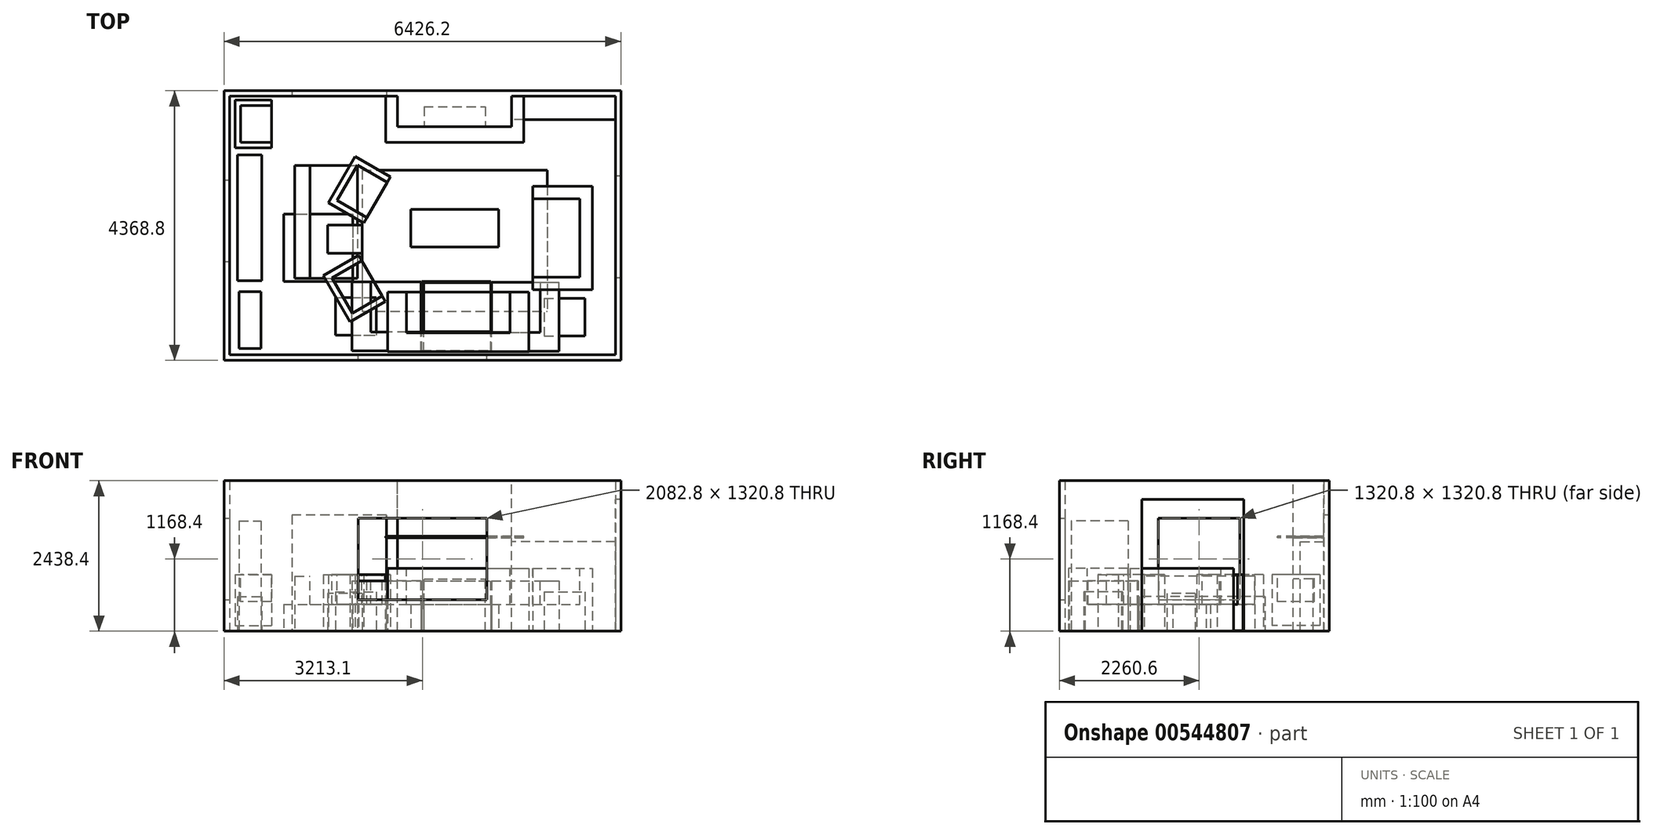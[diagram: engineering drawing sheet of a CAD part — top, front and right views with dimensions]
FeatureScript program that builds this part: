
annotation { "Feature Type Name" : "Feature", "Feature Type Description" : "" }
export const myFeature = defineFeature(function(context is Context, id is Id, definition is map)
    precondition{}
    {
        {
            var Q0;
            Q0=qCreatedBy(makeId("Top.planeOp"),FACE);
            var sketch = newSketch(context, id + "F0", { "sketchPlane" : qUnion([Q0])});
            skLineSegment(sketch, "E0.bottom", {"start": v(0, 0) * mm, "end": v(6248.4, 0) * mm});
            skLineSegment(sketch, "E0.top", {"start": v(0, -4191) * mm, "end": v(6248.4, -4191) * mm});
            skLineSegment(sketch, "E0.left", {"start": v(0, 0) * mm, "end": v(0, -4191) * mm});
            skLineSegment(sketch, "E0.right", {"start": v(6248.4, 0) * mm, "end": v(6248.4, -4191) * mm});
            skLineSegment(sketch, "E1.0", {"start": v(-88.9, 88.9) * mm, "end": v(6337.3, 88.9) * mm});
            skLineSegment(sketch, "E1.1", {"start": v(-88.9, 88.9) * mm, "end": v(-88.9, -4279.9) * mm});
            skLineSegment(sketch, "E1.2", {"start": v(-88.9, -4279.9) * mm, "end": v(6337.3, -4279.9) * mm});
            skLineSegment(sketch, "E1.3", {"start": v(6337.3, 88.9) * mm, "end": v(6337.3, -4279.9) * mm});
            skSolve(sketch);
        }
        {
            var Q0;
            Q0 = qSketchRegion(id + "F0", true);
            extrude(context, id + "F1", {"entities" : qUnion([Q0]), "depth" : 2438.4 * mm, "offsetDistance" : 25.4 * mm});
        }
        {
            var Q0;
            Q0=makeQuery(id+"F1.opExtrude","SWEPT_FACE",FACE,{"disambiguationData":[OSD([sQuery(id+"F0.wireOp",EDGE,"E0.bottom")])]});
            var sketch = newSketch(context, id + "F2", { "sketchPlane" : qUnion([Q0])});
            skLineSegment(sketch, "E2.bottom", {"start": v(1016, 0) * mm, "end": v(2540, 0) * mm});
            skLineSegment(sketch, "E2.top", {"start": v(1016, 1879.6) * mm, "end": v(2540, 1879.6) * mm});
            skLineSegment(sketch, "E2.left", {"start": v(1016, 0) * mm, "end": v(1016, 1879.6) * mm});
            skLineSegment(sketch, "E2.right", {"start": v(2540, 0) * mm, "end": v(2540, 1879.6) * mm});
            skSolve(sketch);
        }
        {
            var Q0;
            Q0 = qSketchRegion(id + "F2", true);
            extrude(context, id + "F3", {"entities" : qUnion([Q0]), "operationType" : NewBodyOperationType.REMOVE, "oppositeDirection" : true, "depth" : 101.6 * mm, "offsetDistance" : 25.4 * mm});
        }
        {
            var Q0;
            Q0=makeQuery(id+"F1.opExtrude","SWEPT_FACE",FACE,{"disambiguationData":[OSD([sQuery(id+"F0.wireOp",EDGE,"E0.bottom")])]});
            var sketch = newSketch(context, id + "F4", { "sketchPlane" : qUnion([Q0])});
            skLineSegment(sketch, "E3.bottom", {"start": v(2717.8, 0) * mm, "end": v(4572, 0) * mm});
            skLineSegment(sketch, "E3.top", {"start": v(2717.8, 2438.4) * mm, "end": v(4572, 2438.4) * mm});
            skLineSegment(sketch, "E3.left", {"start": v(2717.8, 0) * mm, "end": v(2717.8, 2438.4) * mm});
            skLineSegment(sketch, "E3.right", {"start": v(4572, 0) * mm, "end": v(4572, 2438.4) * mm});
            skSolve(sketch);
        }
        {
            var Q0;
            Q0 = qSketchRegion(id + "F4", true);
            extrude(context, id + "F5", {"entities" : qUnion([Q0]), "operationType" : NewBodyOperationType.ADD, "depth" : 495.3 * mm, "offsetDistance" : 25.4 * mm});
        }
        {
            var Q0;
            {var subQ0=sQuery(id+"F0.wireOp",EDGE,"E0.right");var subQ7=sQuery(id+"F0.wireOp",EDGE,"E0.bottom");Q0=makeQuery(id+"F5.boolean.opBoolean","SPLIT",FACE,{"disambiguationData":[TD([makeQuery(id+"F1.opExtrude","SWEPT_FACE",FACE,{"disambiguationData":[OSD([subQ0])]})])],"derivedFrom":makeQuery(id+"F1.opExtrude","SWEPT_FACE",FACE,{"disambiguationData":[OSD([subQ7])]})});}
            var sketch = newSketch(context, id + "F6", { "sketchPlane" : qUnion([Q0])});
            skLineSegment(sketch, "E4.bottom", {"start": v(6248.4, 0) * mm, "end": v(4572, 0) * mm});
            skLineSegment(sketch, "E4.top", {"start": v(6248.4, 1447.8) * mm, "end": v(4572, 1447.8) * mm});
            skLineSegment(sketch, "E4.left", {"start": v(6248.4, 0) * mm, "end": v(6248.4, 1447.8) * mm});
            skLineSegment(sketch, "E4.right", {"start": v(4572, 0) * mm, "end": v(4572, 1447.8) * mm});
            skSolve(sketch);
        }
        {
            var Q0;
            Q0=makeQuery(id+"F6.imprint","IMPRINT",FACE,{"disambiguationData":[TD([[makeQuery(id+"F6.imprint","IMPRINT",EDGE,{"derivedFrom":sQuery(id+"F6.wireOp",EDGE,"E4.bottom")}),1.0]])]});
            extrude(context, id + "F7", {"entities" : qUnion([Q0]), "operationType" : NewBodyOperationType.ADD, "depth" : 381 * mm, "offsetDistance" : 25.4 * mm});
        }
        {
            var Q0;
            Q0=makeQuery(id+"F1.opExtrude","SWEPT_FACE",FACE,{"disambiguationData":[OSD([sQuery(id+"F0.wireOp",EDGE,"E0.top")])]});
            var sketch = newSketch(context, id + "F8", { "sketchPlane" : qUnion([Q0])});
            skLineSegment(sketch, "E5.bottom", {"start": v(-4165.6, 1828.8) * mm, "end": v(-2082.8, 1828.8) * mm});
            skLineSegment(sketch, "E5.top", {"start": v(-4165.6, 508) * mm, "end": v(-2082.8, 508) * mm});
            skLineSegment(sketch, "E5.left", {"start": v(-4165.6, 1828.8) * mm, "end": v(-4165.6, 508) * mm});
            skLineSegment(sketch, "E5.right", {"start": v(-2082.8, 1828.8) * mm, "end": v(-2082.8, 508) * mm});
            skSolve(sketch);
        }
        {
            var Q0;
            Q0=makeQuery(id+"F8.imprint","IMPRINT",FACE,{"disambiguationData":[TD([[makeQuery(id+"F8.imprint","IMPRINT",EDGE,{"derivedFrom":sQuery(id+"F8.wireOp",EDGE,"E5.bottom")}),-1.0]])]});
            extrude(context, id + "F9", {"entities" : qUnion([Q0]), "operationType" : NewBodyOperationType.REMOVE, "endBound" : BoundingType.THROUGH_ALL, "oppositeDirection" : true, "depth" : 25.4 * mm, "offsetDistance" : 25.4 * mm});
        }
        {
            var Q0;
            Q0=makeQuery(id+"F1.opExtrude","SWEPT_FACE",FACE,{"disambiguationData":[OSD([sQuery(id+"F0.wireOp",EDGE,"E0.right")])]});
            var sketch = newSketch(context, id + "F10", { "sketchPlane" : qUnion([Q0])});
            skLineSegment(sketch, "E6.bottom", {"start": v(1295.4, 0) * mm, "end": v(2946.4, 0) * mm});
            skLineSegment(sketch, "E6.top", {"start": v(1295.4, 2133.6) * mm, "end": v(2946.4, 2133.6) * mm});
            skLineSegment(sketch, "E6.left", {"start": v(1295.4, 0) * mm, "end": v(1295.4, 2133.6) * mm});
            skLineSegment(sketch, "E6.right", {"start": v(2946.4, 0) * mm, "end": v(2946.4, 2133.6) * mm});
            skSolve(sketch);
        }
        {
            var Q0;
            Q0=makeQuery(id+"F10.imprint","IMPRINT",FACE,{"disambiguationData":[TD([[makeQuery(id+"F10.imprint","IMPRINT",EDGE,{"derivedFrom":sQuery(id+"F10.wireOp",EDGE,"E6.bottom")}),1.0]])]});
            extrude(context, id + "F11", {"entities" : qUnion([Q0]), "operationType" : NewBodyOperationType.REMOVE, "endBound" : BoundingType.THROUGH_ALL, "oppositeDirection" : true, "depth" : 25.4 * mm, "offsetDistance" : 25.4 * mm});
        }
        {
            var Q0;
            Q0=makeQuery(id+"F1.opExtrude","SWEPT_FACE",FACE,{"disambiguationData":[OSD([sQuery(id+"F0.wireOp",EDGE,"E0.left")])]});
            var sketch = newSketch(context, id + "F12", { "sketchPlane" : qUnion([Q0])});
            skLineSegment(sketch, "E7.bottom", {"start": v(-2679.7, 1828.8) * mm, "end": v(-1358.9, 1828.8) * mm});
            skLineSegment(sketch, "E7.top", {"start": v(-2679.7, 508) * mm, "end": v(-1358.9, 508) * mm});
            skLineSegment(sketch, "E7.left", {"start": v(-2679.7, 1828.8) * mm, "end": v(-2679.7, 508) * mm});
            skLineSegment(sketch, "E7.right", {"start": v(-1358.9, 1828.8) * mm, "end": v(-1358.9, 508) * mm});
            skSolve(sketch);
        }
        {
            var Q0;
            Q0=makeQuery(id+"F12.imprint","IMPRINT",FACE,{"disambiguationData":[TD([[makeQuery(id+"F12.imprint","IMPRINT",EDGE,{"derivedFrom":sQuery(id+"F12.wireOp",EDGE,"E7.bottom")}),-1.0]])]});
            extrude(context, id + "F13", {"entities" : qUnion([Q0]), "operationType" : NewBodyOperationType.REMOVE, "endBound" : BoundingType.THROUGH_ALL, "oppositeDirection" : true, "depth" : 25.4 * mm, "offsetDistance" : 25.4 * mm});
        }
        {
            var Q0;
            Q0=qCreatedBy(makeId("Top.planeOp"),FACE);
            var sketch = newSketch(context, id + "F14", { "sketchPlane" : qUnion([Q0])});
            skLineSegment(sketch, "E8.bottom", {"start": v(127, -952.5) * mm, "end": v(520.7, -952.5) * mm});
            skLineSegment(sketch, "E8.top", {"start": v(127, -2990.85) * mm, "end": v(520.7, -2990.85) * mm});
            skLineSegment(sketch, "E8.left", {"start": v(127, -952.5) * mm, "end": v(127, -2990.85) * mm});
            skLineSegment(sketch, "E8.right", {"start": v(520.7, -952.5) * mm, "end": v(520.7, -2990.85) * mm});
            skSolve(sketch);
        }
        {
            var Q0;
            Q0 = qSketchRegion(id + "F14", true);
            extrude(context, id + "F15", {"entities" : qUnion([Q0]), "depth" : 558.8 * mm, "offsetDistance" : 25.4 * mm});
        }
        {
            var Q0;
            Q0=makeQuery(id+"F5.opExtrude","CAP_FACE",FACE,{"disambiguationData":[OSD([sQuery(id+"F4.wireOp",EDGE,"E3.bottom"),sQuery(id+"F4.wireOp",EDGE,"E3.top"),sQuery(id+"F4.wireOp",EDGE,"E3.left"),sQuery(id+"F4.wireOp",EDGE,"E3.right")])],"isStart":false});
            var sketch = newSketch(context, id + "F16", { "sketchPlane" : qUnion([Q0])});
            skLineSegment(sketch, "E9.bottom", {"start": v(3149.6, 0) * mm, "end": v(4140.2, 0) * mm});
            skLineSegment(sketch, "E9.top", {"start": v(3149.6, 844.55) * mm, "end": v(4140.2, 844.55) * mm});
            skLineSegment(sketch, "E9.left", {"start": v(3149.6, 0) * mm, "end": v(3149.6, 844.55) * mm});
            skLineSegment(sketch, "E9.right", {"start": v(4140.2, 0) * mm, "end": v(4140.2, 844.55) * mm});
            skSolve(sketch);
        }
        {
            var Q0;
            Q0 = qSketchRegion(id + "F16", true);
            extrude(context, id + "F17", {"entities" : qUnion([Q0]), "operationType" : NewBodyOperationType.REMOVE, "oppositeDirection" : true, "depth" : 323.85 * mm, "offsetDistance" : 25.4 * mm});
        }
        {
            var Q0;
            Q0=qCreatedBy(makeId("Top.planeOp"),FACE);
            cPlane(context, id + "F18", {"entities" : qUnion([Q0]), "cplaneType" : CPlaneType.OFFSET, "offset" : 1536.7 * mm, "width" : 152.4 * mm, "height" : 152.4 * mm});
        }
        {
            var Q0;
            Q0=qCreatedBy(id+"F18.planeOp",FACE);
            var sketch = newSketch(context, id + "F19", { "sketchPlane" : qUnion([Q0])});
            skLineSegment(sketch, "E10.0", {"start": v(2540, 0) * mm, "end": v(2717.8, 0) * mm});
            skLineSegment(sketch, "E11", {"start": v(2717.8, 0) * mm, "end": v(2527.3, 0) * mm});
            skLineSegment(sketch, "E12", {"start": v(2527.3, 0) * mm, "end": v(2527.3, -749.3) * mm});
            skLineSegment(sketch, "E13", {"start": v(2527.3, -749.3) * mm, "end": v(4762.5, -749.3) * mm});
            skLineSegment(sketch, "E14", {"start": v(4762.5, -749.3) * mm, "end": v(4762.5, 0) * mm});
            skPoint(sketch, "E15.0", {"position": v(4572, 0) * mm});
            skPoint(sketch, "E16.0", {"position": v(4572, -495.3) * mm});
            skPoint(sketch, "E17.0", {"position": v(2717.8, -495.3) * mm});
            skLineSegment(sketch, "E18", {"start": v(4762.5, 0) * mm, "end": v(4572, 0) * mm});
            skLineSegment(sketch, "E19", {"start": v(4572, -495.3) * mm, "end": v(2717.8, -495.3) * mm});
            skLineSegment(sketch, "E20", {"start": v(2717.8, -495.3) * mm, "end": v(2717.8, 0) * mm});
            skLineSegment(sketch, "E21", {"start": v(4572, 0) * mm, "end": v(4572, -495.3) * mm});
            skSolve(sketch);
        }
        {
            var Q0;
            {var subQ0=sQuery(id+"F19.wireOp",EDGE,"E12");Q0=makeQuery(id+"F19.imprint","IMPRINT",FACE,{"disambiguationData":[TD([[makeQuery(id+"F19.imprint","IMPRINT",EDGE,{"derivedFrom":subQ0}),1.0]])]});}
            extrude(context, id + "F20", {"entities" : qUnion([Q0]), "operationType" : NewBodyOperationType.ADD, "oppositeDirection" : true, "depth" : 25.4 * mm, "offsetDistance" : 25.4 * mm});
        }
        {
            var Q0;
            Q0=qCreatedBy(makeId("Top.planeOp"),FACE);
            var sketch = newSketch(context, id + "F21", { "sketchPlane" : qUnion([Q0])});
            skLineSegment(sketch, "E22.bottom", {"start": v(6850.74, -4489.71) * mm, "end": v(7968.34, -4489.71) * mm});
            skLineSegment(sketch, "E22.top", {"start": v(6850.74, -3372.11) * mm, "end": v(7968.34, -3372.11) * mm});
            skLineSegment(sketch, "E22.left", {"start": v(6850.74, -4489.71) * mm, "end": v(6850.74, -3372.11) * mm});
            skLineSegment(sketch, "E22.right", {"start": v(7968.34, -4489.71) * mm, "end": v(7968.34, -3372.11) * mm});
            skLineSegment(sketch, "E23.bottom", {"start": v(7986.57, -4486.73) * mm, "end": v(9104.17, -4486.73) * mm});
            skLineSegment(sketch, "E23.top", {"start": v(7986.57, -3369.13) * mm, "end": v(9104.17, -3369.13) * mm});
            skLineSegment(sketch, "E23.left", {"start": v(7986.57, -4486.73) * mm, "end": v(7986.57, -3369.13) * mm});
            skLineSegment(sketch, "E23.right", {"start": v(9104.17, -4486.73) * mm, "end": v(9104.17, -3369.13) * mm});
            skLineSegment(sketch, "E24.bottom", {"start": v(9113.11, -4490.55) * mm, "end": v(10205.31, -4490.55) * mm});
            skLineSegment(sketch, "E24.top", {"start": v(9113.11, -3372.95) * mm, "end": v(10205.31, -3372.95) * mm});
            skLineSegment(sketch, "E24.left", {"start": v(9113.11, -4490.55) * mm, "end": v(9113.11, -3372.95) * mm});
            skLineSegment(sketch, "E24.right", {"start": v(10205.31, -4490.55) * mm, "end": v(10205.31, -3372.95) * mm});
            skLineSegment(sketch, "E25.bottom", {"start": v(10216.89, -4488.37) * mm, "end": v(11309.09, -4488.37) * mm});
            skLineSegment(sketch, "E25.top", {"start": v(10216.89, -3370.77) * mm, "end": v(11309.09, -3370.77) * mm});
            skLineSegment(sketch, "E25.left", {"start": v(10216.89, -4488.37) * mm, "end": v(10216.89, -3370.77) * mm});
            skLineSegment(sketch, "E25.right", {"start": v(11309.09, -4488.37) * mm, "end": v(11309.09, -3370.77) * mm});
            skSolve(sketch);
        }
        {
            var Q0;
            Q0 = qSketchRegion(id + "F21", true);
            extrude(context, id + "F22", {"entities" : qUnion([Q0]), "depth" : 812.8 * mm, "offsetDistance" : 25.4 * mm});
        }
        {
            var Q0;
            Q0=makeQuery(id+"F22.opExtrude","CAP_FACE",FACE,{"disambiguationData":[OSD([sQuery(id+"F21.wireOp",EDGE,"E22.bottom"),sQuery(id+"F21.wireOp",EDGE,"E22.top"),sQuery(id+"F21.wireOp",EDGE,"E22.left"),sQuery(id+"F21.wireOp",EDGE,"E22.right")])],"isStart":false});
            var sketch = newSketch(context, id + "F23", { "sketchPlane" : qUnion([Q0])});
            skLineSegment(sketch, "E26.bottom", {"start": v(7968.34, -3372.11) * mm, "end": v(7155.54, -3372.11) * mm});
            skLineSegment(sketch, "E26.top", {"start": v(7968.34, -4184.91) * mm, "end": v(7155.54, -4184.91) * mm});
            skLineSegment(sketch, "E26.left", {"start": v(7968.34, -3372.11) * mm, "end": v(7968.34, -4184.91) * mm});
            skLineSegment(sketch, "E26.right", {"start": v(7155.54, -3372.11) * mm, "end": v(7155.54, -4184.91) * mm});
            skPoint(sketch, "E27.0", {"position": v(7986.57, -3369.13) * mm});
            skPoint(sketch, "E28.0", {"position": v(9104.17, -3369.13) * mm});
            skPoint(sketch, "E29.0", {"position": v(9113.11, -3372.95) * mm});
            skPoint(sketch, "E30.0", {"position": v(10205.31, -3372.95) * mm});
            skPoint(sketch, "E31.0", {"position": v(10216.89, -3370.77) * mm});
            skLineSegment(sketch, "E32.bottom", {"start": v(7986.57, -3369.13) * mm, "end": v(9104.17, -3369.13) * mm});
            skLineSegment(sketch, "E32.top", {"start": v(7986.57, -4181.93) * mm, "end": v(9104.17, -4181.93) * mm});
            skLineSegment(sketch, "E32.left", {"start": v(7986.57, -3369.13) * mm, "end": v(7986.57, -4181.93) * mm});
            skLineSegment(sketch, "E32.right", {"start": v(9104.17, -3369.13) * mm, "end": v(9104.17, -4181.93) * mm});
            skLineSegment(sketch, "E33.bottom", {"start": v(9113.11, -3372.95) * mm, "end": v(10205.31, -3372.95) * mm});
            skLineSegment(sketch, "E33.top", {"start": v(9113.11, -4185.75) * mm, "end": v(10205.31, -4185.75) * mm});
            skLineSegment(sketch, "E33.left", {"start": v(9113.11, -3372.95) * mm, "end": v(9113.11, -4185.75) * mm});
            skLineSegment(sketch, "E33.right", {"start": v(10205.31, -3372.95) * mm, "end": v(10205.31, -4185.75) * mm});
            skLineSegment(sketch, "E34.bottom", {"start": v(10216.89, -3370.77) * mm, "end": v(11004.29, -3370.77) * mm});
            skLineSegment(sketch, "E34.top", {"start": v(10216.89, -4183.57) * mm, "end": v(11004.29, -4183.57) * mm});
            skLineSegment(sketch, "E34.left", {"start": v(10216.89, -3370.77) * mm, "end": v(10216.89, -4183.57) * mm});
            skLineSegment(sketch, "E34.right", {"start": v(11004.29, -3370.77) * mm, "end": v(11004.29, -4183.57) * mm});
            skSolve(sketch);
        }
        {
            var Q0;
            Q0 = qSketchRegion(id + "F23", true);
            extrude(context, id + "F24", {"entities" : qUnion([Q0]), "operationType" : NewBodyOperationType.REMOVE, "oppositeDirection" : true, "depth" : 381 * mm, "offsetDistance" : 25.4 * mm});
        }
        {
            var Q0;
            Q0=qCreatedBy(makeId("Top.planeOp"),FACE);
            var sketch = newSketch(context, id + "F25", { "sketchPlane" : qUnion([Q0])});
            skLineSegment(sketch, "E35.bottom", {"start": v(6846.18, -2262.85) * mm, "end": v(7963.78, -2262.85) * mm});
            skLineSegment(sketch, "E35.top", {"start": v(6846.18, -3355.05) * mm, "end": v(7963.78, -3355.05) * mm});
            skLineSegment(sketch, "E35.left", {"start": v(6846.18, -2262.85) * mm, "end": v(6846.18, -3355.05) * mm});
            skLineSegment(sketch, "E35.right", {"start": v(7963.78, -2262.85) * mm, "end": v(7963.78, -3355.05) * mm});
            skSolve(sketch);
        }
        {
            var Q0;
            Q0 = qSketchRegion(id + "F25", true);
            extrude(context, id + "F26", {"entities" : qUnion([Q0]), "depth" : 431.8 * mm, "offsetDistance" : 25.4 * mm});
        }
        {
            var Q0;
            Q0=makeQuery(id+"F22.opExtrude","SWEPT_BODY",BODY,{"disambiguationData":[OSD([sQuery(id+"F21.wireOp",EDGE,"E22.bottom"),sQuery(id+"F21.wireOp",EDGE,"E22.top"),sQuery(id+"F21.wireOp",EDGE,"E22.left"),sQuery(id+"F21.wireOp",EDGE,"E22.right")])]});
            var Q1;
            Q1=makeQuery(id+"F22.opExtrude","SWEPT_BODY",BODY,{"disambiguationData":[OSD([sQuery(id+"F21.wireOp",EDGE,"E24.bottom"),sQuery(id+"F21.wireOp",EDGE,"E24.top"),sQuery(id+"F21.wireOp",EDGE,"E24.left"),sQuery(id+"F21.wireOp",EDGE,"E24.right")])]});
            var Q2;
            Q2=makeQuery(id+"F22.opExtrude","SWEPT_BODY",BODY,{"disambiguationData":[OSD([sQuery(id+"F21.wireOp",EDGE,"E23.bottom"),sQuery(id+"F21.wireOp",EDGE,"E23.top"),sQuery(id+"F21.wireOp",EDGE,"E23.left"),sQuery(id+"F21.wireOp",EDGE,"E23.right")])]});
            var Q3;
            Q3=makeQuery(id+"F22.opExtrude","SWEPT_BODY",BODY,{"disambiguationData":[OSD([sQuery(id+"F21.wireOp",EDGE,"E25.bottom"),sQuery(id+"F21.wireOp",EDGE,"E25.top"),sQuery(id+"F21.wireOp",EDGE,"E25.left"),sQuery(id+"F21.wireOp",EDGE,"E25.right")])]});
            var Q4;
            Q4=makeQuery(id+"F26.opExtrude","SWEPT_BODY",BODY,{"disambiguationData":[OSD([sQuery(id+"F25.wireOp",EDGE,"E35.bottom"),sQuery(id+"F25.wireOp",EDGE,"E35.top"),sQuery(id+"F25.wireOp",EDGE,"E35.left"),sQuery(id+"F25.wireOp",EDGE,"E35.right")])]});
            var Q5;
            Q5=makeQuery(id+"F26.opExtrude","SWEPT_BODY",BODY,{"disambiguationData":[OSD([sQuery(id+"F25.wireOp",EDGE,"f7MXd3Yk-BWBa-OAzn-Fjwn-ZuBZJERHKitf.bottom"),sQuery(id+"F25.wireOp",EDGE,"f7MXd3Yk-BWBa-OAzn-Fjwn-ZuBZJERHKitf.top"),sQuery(id+"F25.wireOp",EDGE,"f7MXd3Yk-BWBa-OAzn-Fjwn-ZuBZJERHKitf.left"),sQuery(id+"F25.wireOp",EDGE,"f7MXd3Yk-BWBa-OAzn-Fjwn-ZuBZJERHKitf.right")])]});
            var Q6;
            Q6=makeQuery(id+"F22.opExtrude","CAP_VERTEX",VERTEX,{"disambiguationData":[OSD([sQuery(id+"F21.wireOp",EDGE,"E22.bottom"),sQuery(id+"F21.wireOp",EDGE,"E22.left")])],"isStart":false});
            transform(context, id + "F27", {"entities" : qUnion([Q0, Q1, Q2, Q3, Q4, Q5]), "transformType" : TransformType.TRANSLATION_3D, "dx" : -5969 * mm, "dy" : 355.6 * mm, "dz" : 0 * mm, "makeCopy" : false});
        }
        {
            var Q0;
            Q0=makeQuery(id+"F22.opExtrude","SWEPT_BODY",BODY,{"disambiguationData":[OSD([sQuery(id+"F21.wireOp",EDGE,"E22.bottom"),sQuery(id+"F21.wireOp",EDGE,"E22.top"),sQuery(id+"F21.wireOp",EDGE,"E22.left"),sQuery(id+"F21.wireOp",EDGE,"E22.right")])]});
            var Q1;
            Q1=makeQuery(id+"F22.opExtrude","SWEPT_BODY",BODY,{"disambiguationData":[OSD([sQuery(id+"F21.wireOp",EDGE,"E23.bottom"),sQuery(id+"F21.wireOp",EDGE,"E23.top"),sQuery(id+"F21.wireOp",EDGE,"E23.left"),sQuery(id+"F21.wireOp",EDGE,"E23.right")])]});
            transform(context, id + "F28", {"entities" : qUnion([Q0, Q1]), "transformType" : TransformType.TRANSLATION_3D, "dx" : 1099.82 * mm, "dy" : 10.16 * mm, "dz" : 0 * mm, "makeCopy" : false});
        }
        {
            var Q0;
            Q0=qCreatedBy(makeId("Top.planeOp"),FACE);
            var sketch = newSketch(context, id + "F29", { "sketchPlane" : qUnion([Q0])});
            skLineSegment(sketch, "E36.0", {"start": v(0, -4191) * mm, "end": v(6248.4, -4191) * mm});
            skLineSegment(sketch, "E37.bottom", {"start": v(2146.3, -1200.15) * mm, "end": v(5143.5, -1200.15) * mm});
            skLineSegment(sketch, "E37.top", {"start": v(2146.3, -3486.15) * mm, "end": v(5143.5, -3486.15) * mm});
            skLineSegment(sketch, "E37.left", {"start": v(2146.3, -1200.15) * mm, "end": v(2146.3, -3486.15) * mm});
            skLineSegment(sketch, "E37.right", {"start": v(5143.5, -1200.15) * mm, "end": v(5143.5, -3486.15) * mm});
            skPoint(sketch, "E37.middle", {"position": v(3644.9, -2343.15) * mm});
            skPoint(sketch, "E38.0", {"position": v(3644.9, -495.3) * mm});
            skLineSegment(sketch, "E39", {"start": v(3644.9, -495.3) * mm, "end": v(3644.9, -4191) * mm, "construction": true});
            skSolve(sketch);
        }
        {
            var Q0;
            Q0 = qSketchRegion(id + "F29", true);
            extrude(context, id + "F30", {"entities" : qUnion([Q0]), "depth" : 6.35 * mm, "offsetDistance" : 25.4 * mm});
        }
        {
            var Q0;
            Q0=qCreatedBy(makeId("Top.planeOp"),FACE);
            var sketch = newSketch(context, id + "F31", { "sketchPlane" : qUnion([Q0])});
            skPoint(sketch, "E40.0", {"position": v(4762.5, -749.3) * mm});
            skPoint(sketch, "E41.0", {"position": v(2717.8, -495.3) * mm});
            skLineSegment(sketch, "E42.bottom", {"start": v(2717.8, -495.3) * mm, "end": v(4572, -495.3) * mm});
            skLineSegment(sketch, "E42.top", {"start": v(2717.8, -1060.45) * mm, "end": v(4572, -1060.45) * mm});
            skLineSegment(sketch, "E42.left", {"start": v(2717.8, -495.3) * mm, "end": v(2717.8, -1060.45) * mm});
            skLineSegment(sketch, "E42.right", {"start": v(4572, -495.3) * mm, "end": v(4572, -1060.45) * mm});
            skSolve(sketch);
        }
        {
            var Q0;
            Q0=qCreatedBy(makeId("Top.planeOp"),FACE);
            var sketch = newSketch(context, id + "F32", { "sketchPlane" : qUnion([Q0])});
            skPoint(sketch, "E43.0", {"position": v(3644.9, -495.3) * mm});
            skLineSegment(sketch, "E44.0", {"start": v(0, -4191) * mm, "end": v(6248.4, -4191) * mm});
            skLineSegment(sketch, "E45", {"start": v(3644.9, -495.3) * mm, "end": v(3644.9, -4191) * mm, "construction": true});
            skLineSegment(sketch, "E46.bottom", {"start": v(2933.7, -2443.78) * mm, "end": v(4356.1, -2443.78) * mm});
            skLineSegment(sketch, "E46.top", {"start": v(2933.7, -1834.18) * mm, "end": v(4356.1, -1834.18) * mm});
            skLineSegment(sketch, "E46.left", {"start": v(2933.7, -2443.78) * mm, "end": v(2933.7, -1834.18) * mm});
            skLineSegment(sketch, "E46.right", {"start": v(4356.1, -2443.78) * mm, "end": v(4356.1, -1834.18) * mm});
            skPoint(sketch, "E46.middle", {"position": v(3644.9, -2138.98) * mm});
            skSolve(sketch);
        }
        {
            var Q0;
            Q0 = qSketchRegion(id + "F32", true);
            extrude(context, id + "F33", {"entities" : qUnion([Q0]), "depth" : 431.8 * mm, "offsetDistance" : 25.4 * mm});
        }
        {
            var Q0;
            Q0=qCreatedBy(makeId("Top.planeOp"),FACE);
            var sketch = newSketch(context, id + "F34", { "sketchPlane" : qUnion([Q0])});
            skLineSegment(sketch, "E47.bottom", {"start": v(7186.66, -2268.3) * mm, "end": v(9472.66, -2268.3) * mm});
            skLineSegment(sketch, "E47.top", {"start": v(7186.66, -3233.5) * mm, "end": v(9472.66, -3233.5) * mm});
            skLineSegment(sketch, "E47.left", {"start": v(7186.66, -2268.3) * mm, "end": v(7186.66, -3233.5) * mm});
            skLineSegment(sketch, "E47.right", {"start": v(9472.66, -2268.3) * mm, "end": v(9472.66, -3233.5) * mm});
            skSolve(sketch);
        }
        {
            var Q0;
            Q0 = qSketchRegion(id + "F34", true);
            extrude(context, id + "F35", {"entities" : qUnion([Q0]), "depth" : 1016 * mm, "offsetDistance" : 25.4 * mm});
        }
        {
            var Q0;
            Q0=makeQuery(id+"F35.opExtrude","CAP_FACE",FACE,{"disambiguationData":[OSD([sQuery(id+"F34.wireOp",EDGE,"E47.bottom"),sQuery(id+"F34.wireOp",EDGE,"E47.top"),sQuery(id+"F34.wireOp",EDGE,"E47.left"),sQuery(id+"F34.wireOp",EDGE,"E47.right")])],"isStart":false});
            var sketch = newSketch(context, id + "F36", { "sketchPlane" : qUnion([Q0])});
            skLineSegment(sketch, "E48.bottom", {"start": v(7491.46, -2268.3) * mm, "end": v(9167.86, -2268.3) * mm});
            skLineSegment(sketch, "E48.top", {"start": v(7491.46, -2928.7) * mm, "end": v(9167.86, -2928.7) * mm});
            skLineSegment(sketch, "E48.left", {"start": v(7491.46, -2268.3) * mm, "end": v(7491.46, -2928.7) * mm});
            skLineSegment(sketch, "E48.right", {"start": v(9167.86, -2268.3) * mm, "end": v(9167.86, -2928.7) * mm});
            skSolve(sketch);
        }
        {
            var Q0;
            Q0 = qSketchRegion(id + "F36", true);
            extrude(context, id + "F37", {"entities" : qUnion([Q0]), "operationType" : NewBodyOperationType.REMOVE, "oppositeDirection" : true, "depth" : 584.2 * mm, "offsetDistance" : 25.4 * mm});
        }
        {
            var Q0;
            Q0=makeQuery(id+"F35.opExtrude","SWEPT_BODY",BODY,{"disambiguationData":[OSD([sQuery(id+"F34.wireOp",EDGE,"E47.bottom"),sQuery(id+"F34.wireOp",EDGE,"E47.top"),sQuery(id+"F34.wireOp",EDGE,"E47.left"),sQuery(id+"F34.wireOp",EDGE,"E47.right")])]});
            transform(context, id + "F38", {"entities" : qUnion([Q0]), "transformType" : TransformType.TRANSLATION_3D, "dx" : -4622.8 * mm, "dy" : -901.7 * mm, "dz" : 0 * mm, "makeCopy" : false});
        }
        {
            var Q0;
            Q0=makeQuery(id+"F35.opExtrude","SWEPT_BODY",BODY,{"disambiguationData":[OSD([sQuery(id+"F34.wireOp",EDGE,"E47.bottom"),sQuery(id+"F34.wireOp",EDGE,"E47.top"),sQuery(id+"F34.wireOp",EDGE,"E47.left"),sQuery(id+"F34.wireOp",EDGE,"E47.right")])]});
            transform(context, id + "F39", {"entities" : qUnion([Q0]), "transformType" : TransformType.TRANSLATION_3D, "dx" : 1412.24 * mm, "dy" : 1518.92 * mm, "dz" : 0 * mm, "makeCopy" : true});
        }
        {
            var Q0;
            Q0=makeQuery(id+"F39.opPattern","COPY",BODY,{"derivedFrom":makeQuery(id+"F35.opExtrude","SWEPT_BODY",BODY,{"disambiguationData":[OSD([sQuery(id+"F34.wireOp",EDGE,"E47.bottom"),sQuery(id+"F34.wireOp",EDGE,"E47.top"),sQuery(id+"F34.wireOp",EDGE,"E47.left"),sQuery(id+"F34.wireOp",EDGE,"E47.right")])]}),"instanceName":"1"});
            var Q1;
            Q1=makeQuery(id+"F39.opPattern","COPY",EDGE,{"derivedFrom":makeQuery(id+"F35.opExtrude","SWEPT_EDGE",EDGE,{"disambiguationData":[OSD([sQuery(id+"F34.wireOp",EDGE,"E47.top"),sQuery(id+"F34.wireOp",EDGE,"E47.right")])]}),"instanceName":"1"});
            transform(context, id + "F40", {"entities" : qUnion([Q0]), "transformType" : TransformType.ROTATION, "transformAxis" : qUnion([Q1]), "angle" : 270 * degree, "makeCopy" : false});
        }
        {
            var Q0;
            Q0=makeQuery(id+"F39.opPattern","COPY",BODY,{"derivedFrom":makeQuery(id+"F35.opExtrude","SWEPT_BODY",BODY,{"disambiguationData":[OSD([sQuery(id+"F34.wireOp",EDGE,"E47.bottom"),sQuery(id+"F34.wireOp",EDGE,"E47.top"),sQuery(id+"F34.wireOp",EDGE,"E47.left"),sQuery(id+"F34.wireOp",EDGE,"E47.right")])]}),"instanceName":"1"});
            transform(context, id + "F41", {"entities" : qUnion([Q0]), "transformType" : TransformType.TRANSLATION_3D, "dx" : -452.12 * mm, "dy" : 1783.08 * mm, "dz" : 0 * mm, "makeCopy" : false});
        }
        {
            var Q0;
            Q0=makeQuery(id+"F39.opPattern","COPY",BODY,{"derivedFrom":makeQuery(id+"F35.opExtrude","SWEPT_BODY",BODY,{"disambiguationData":[OSD([sQuery(id+"F34.wireOp",EDGE,"E47.bottom"),sQuery(id+"F34.wireOp",EDGE,"E47.top"),sQuery(id+"F34.wireOp",EDGE,"E47.left"),sQuery(id+"F34.wireOp",EDGE,"E47.right")])]}),"instanceName":"1"});
            deleteBodies(context, id + "F42", {"entities" : qUnion([Q0])});
        }
        {
            var Q0;
            Q0=qCreatedBy(makeId("Top.planeOp"),FACE);
            var sketch = newSketch(context, id + "F43", { "sketchPlane" : qUnion([Q0])});
            skPoint(sketch, "E49.0", {"position": v(4849.86, -3170) * mm});
            skLineSegment(sketch, "E50.bottom", {"start": v(5031.25, -2866.95) * mm, "end": v(5996.45, -2866.95) * mm});
            skLineSegment(sketch, "E50.top", {"start": v(5031.25, -1190.55) * mm, "end": v(5996.45, -1190.55) * mm});
            skLineSegment(sketch, "E50.left", {"start": v(5031.25, -2866.95) * mm, "end": v(5031.25, -1190.55) * mm});
            skLineSegment(sketch, "E50.right", {"start": v(5996.45, -2866.95) * mm, "end": v(5996.45, -1190.55) * mm});
            skSolve(sketch);
        }
        {
            var Q0;
            Q0 = qSketchRegion(id + "F43", true);
            extrude(context, id + "F44", {"entities" : qUnion([Q0]), "depth" : 1016 * mm, "offsetDistance" : 25.4 * mm});
        }
        {
            var Q0;
            Q0=makeQuery(id+"F44.opExtrude","CAP_FACE",FACE,{"disambiguationData":[OSD([sQuery(id+"F43.wireOp",EDGE,"E50.bottom"),sQuery(id+"F43.wireOp",EDGE,"E50.top"),sQuery(id+"F43.wireOp",EDGE,"E50.left"),sQuery(id+"F43.wireOp",EDGE,"E50.right")])],"isStart":false});
            var sketch = newSketch(context, id + "F45", { "sketchPlane" : qUnion([Q0])});
            skLineSegment(sketch, "E51.bottom", {"start": v(5031.25, -1393.75) * mm, "end": v(5793.25, -1393.75) * mm});
            skLineSegment(sketch, "E51.top", {"start": v(5031.25, -2663.75) * mm, "end": v(5793.25, -2663.75) * mm});
            skLineSegment(sketch, "E51.left", {"start": v(5031.25, -1393.75) * mm, "end": v(5031.25, -2663.75) * mm});
            skLineSegment(sketch, "E51.right", {"start": v(5793.25, -1393.75) * mm, "end": v(5793.25, -2663.75) * mm});
            skSolve(sketch);
        }
        {
            var Q0;
            Q0 = qSketchRegion(id + "F45", true);
            extrude(context, id + "F46", {"entities" : qUnion([Q0]), "operationType" : NewBodyOperationType.REMOVE, "oppositeDirection" : true, "depth" : 584.2 * mm, "offsetDistance" : 25.4 * mm});
        }
        {
            var Q0;
            Q0=qCreatedBy(makeId("Top.planeOp"),FACE);
            var sketch = newSketch(context, id + "F47", { "sketchPlane" : qUnion([Q0])});
            skLineSegment(sketch, "E52.bottom", {"start": v(1059.6, -1118.6) * mm, "end": v(2075.6, -1118.6) * mm});
            skLineSegment(sketch, "E52.top", {"start": v(1059.6, -2947.4) * mm, "end": v(2075.6, -2947.4) * mm});
            skLineSegment(sketch, "E52.left", {"start": v(1059.6, -1118.6) * mm, "end": v(1059.6, -2947.4) * mm});
            skLineSegment(sketch, "E52.right", {"start": v(2075.6, -1118.6) * mm, "end": v(2075.6, -2947.4) * mm});
            skSolve(sketch);
        }
        {
            var Q0;
            Q0 = qSketchRegion(id + "F47", true);
            extrude(context, id + "F48", {"entities" : qUnion([Q0]), "depth" : 889 * mm, "offsetDistance" : 25.4 * mm});
        }
        {
            var Q0;
            Q0=makeQuery(id+"F48.opExtrude","CAP_FACE",FACE,{"disambiguationData":[OSD([sQuery(id+"F47.wireOp",EDGE,"E52.bottom"),sQuery(id+"F47.wireOp",EDGE,"E52.top"),sQuery(id+"F47.wireOp",EDGE,"E52.left"),sQuery(id+"F47.wireOp",EDGE,"E52.right")])],"isStart":false});
            var sketch = newSketch(context, id + "F49", { "sketchPlane" : qUnion([Q0])});
            skLineSegment(sketch, "E53.bottom", {"start": v(2075.6, -1118.6) * mm, "end": v(1306.15, -1118.6) * mm});
            skLineSegment(sketch, "E53.top", {"start": v(2075.6, -2947.4) * mm, "end": v(1306.15, -2947.4) * mm});
            skLineSegment(sketch, "E53.left", {"start": v(2075.6, -1118.6) * mm, "end": v(2075.6, -2947.4) * mm});
            skLineSegment(sketch, "E53.right", {"start": v(1306.15, -1118.6) * mm, "end": v(1306.15, -2947.4) * mm});
            skSolve(sketch);
        }
        {
            var Q0;
            Q0 = qSketchRegion(id + "F49", true);
            extrude(context, id + "F50", {"entities" : qUnion([Q0]), "operationType" : NewBodyOperationType.REMOVE, "oppositeDirection" : true, "depth" : 457.2 * mm, "offsetDistance" : 25.4 * mm});
        }
        {
            var Q0;
            Q0=makeQuery(id+"F44.opExtrude","SWEPT_BODY",BODY,{"disambiguationData":[OSD([sQuery(id+"F43.wireOp",EDGE,"E50.bottom"),sQuery(id+"F43.wireOp",EDGE,"E50.top"),sQuery(id+"F43.wireOp",EDGE,"E50.left"),sQuery(id+"F43.wireOp",EDGE,"E50.right")])]});
            transform(context, id + "F51", {"entities" : qUnion([Q0]), "transformType" : TransformType.TRANSLATION_3D, "dx" : -119.38 * mm, "dy" : -266.7 * mm, "dz" : 0 * mm, "makeCopy" : false});
        }
        {
            var Q0;
            Q0=qCreatedBy(makeId("Top.planeOp"),FACE);
            var sketch = newSketch(context, id + "F52", { "sketchPlane" : qUnion([Q0])});
            skLineSegment(sketch, "E54.bottom", {"start": v(1514.75, -1190.86) * mm, "end": v(2175.15, -1190.86) * mm});
            skLineSegment(sketch, "E54.top", {"start": v(1514.75, -2054.46) * mm, "end": v(2175.15, -2054.46) * mm});
            skLineSegment(sketch, "E54.left", {"start": v(1514.75, -1190.86) * mm, "end": v(1514.75, -2054.46) * mm});
            skLineSegment(sketch, "E54.right", {"start": v(2175.15, -1190.86) * mm, "end": v(2175.15, -2054.46) * mm});
            skSolve(sketch);
        }
        {
            var Q0;
            Q0 = qSketchRegion(id + "F52", true);
            extrude(context, id + "F53", {"entities" : qUnion([Q0]), "depth" : 914.4 * mm, "offsetDistance" : 25.4 * mm});
        }
        {
            var Q0;
            Q0=makeQuery(id+"F53.opExtrude","CAP_FACE",FACE,{"disambiguationData":[OSD([sQuery(id+"F52.wireOp",EDGE,"E54.bottom"),sQuery(id+"F52.wireOp",EDGE,"E54.top"),sQuery(id+"F52.wireOp",EDGE,"E54.left"),sQuery(id+"F52.wireOp",EDGE,"E54.right")])],"isStart":false});
            var sketch = newSketch(context, id + "F54", { "sketchPlane" : qUnion([Q0])});
            skLineSegment(sketch, "E55.bottom", {"start": v(2175.15, -1292.46) * mm, "end": v(1616.35, -1292.46) * mm});
            skLineSegment(sketch, "E55.top", {"start": v(2175.15, -1952.86) * mm, "end": v(1616.35, -1952.86) * mm});
            skLineSegment(sketch, "E55.left", {"start": v(2175.15, -1292.46) * mm, "end": v(2175.15, -1952.86) * mm});
            skLineSegment(sketch, "E55.right", {"start": v(1616.35, -1292.46) * mm, "end": v(1616.35, -1952.86) * mm});
            skSolve(sketch);
        }
        {
            var Q0;
            Q0 = qSketchRegion(id + "F54", true);
            extrude(context, id + "F55", {"entities" : qUnion([Q0]), "operationType" : NewBodyOperationType.REMOVE, "oppositeDirection" : true, "depth" : 482.6 * mm, "offsetDistance" : 25.4 * mm});
        }
        {
            var Q0;
            Q0=makeQuery(id+"F53.opExtrude","SWEPT_BODY",BODY,{"disambiguationData":[OSD([sQuery(id+"F52.wireOp",EDGE,"E54.bottom"),sQuery(id+"F52.wireOp",EDGE,"E54.top"),sQuery(id+"F52.wireOp",EDGE,"E54.left"),sQuery(id+"F52.wireOp",EDGE,"E54.right")])]});
            transform(context, id + "F56", {"entities" : qUnion([Q0]), "transformType" : TransformType.TRANSLATION_3D, "dx" : 152.4 * mm, "dy" : -1330.96 * mm, "dz" : 0 * mm, "makeCopy" : true});
        }
        {
            var Q0;
            Q0=qCreatedBy(makeId("Top.planeOp"),FACE);
            var sketch = newSketch(context, id + "F57", { "sketchPlane" : qUnion([Q0])});
            skLineSegment(sketch, "E56.bottom", {"start": v(5095.77, -3274.58) * mm, "end": v(5756.17, -3274.58) * mm});
            skLineSegment(sketch, "E56.top", {"start": v(5095.77, -3884.18) * mm, "end": v(5756.17, -3884.18) * mm});
            skLineSegment(sketch, "E56.left", {"start": v(5095.77, -3274.58) * mm, "end": v(5095.77, -3884.18) * mm});
            skLineSegment(sketch, "E56.right", {"start": v(5756.17, -3274.58) * mm, "end": v(5756.17, -3884.18) * mm});
            skSolve(sketch);
        }
        {
            var Q0;
            Q0 = qSketchRegion(id + "F57", true);
            extrude(context, id + "F58", {"entities" : qUnion([Q0]), "depth" : 635 * mm, "offsetDistance" : 25.4 * mm});
        }
        {
            var Q0;
            Q0=makeQuery(id+"F58.opExtrude","SWEPT_BODY",BODY,{"disambiguationData":[OSD([sQuery(id+"F57.wireOp",EDGE,"E56.bottom"),sQuery(id+"F57.wireOp",EDGE,"E56.top"),sQuery(id+"F57.wireOp",EDGE,"E56.left"),sQuery(id+"F57.wireOp",EDGE,"E56.right")])]});
            transform(context, id + "F59", {"entities" : qUnion([Q0]), "transformType" : TransformType.TRANSLATION_3D, "dx" : -3380.74 * mm, "dy" : 15.24 * mm, "dz" : 0 * mm, "makeCopy" : true});
        }
        {
            var Q0;
            Q0=makeQuery(id+"F56.opPattern","COPY",BODY,{"derivedFrom":makeQuery(id+"F53.opExtrude","SWEPT_BODY",BODY,{"disambiguationData":[OSD([sQuery(id+"F52.wireOp",EDGE,"E54.bottom"),sQuery(id+"F52.wireOp",EDGE,"E54.top"),sQuery(id+"F52.wireOp",EDGE,"E54.left"),sQuery(id+"F52.wireOp",EDGE,"E54.right")])]}),"instanceName":"1"});
            transform(context, id + "F60", {"entities" : qUnion([Q0]), "transformType" : TransformType.TRANSLATION_3D, "dx" : -1577.34 * mm, "dy" : 2461.26 * mm, "dz" : 0 * mm, "makeCopy" : true});
        }
        {
            var Q0;
            Q0=makeQuery(id+"F60.opPattern","COPY",BODY,{"derivedFrom":makeQuery(id+"F56.opPattern","COPY",BODY,{"derivedFrom":makeQuery(id+"F53.opExtrude","SWEPT_BODY",BODY,{"disambiguationData":[OSD([sQuery(id+"F52.wireOp",EDGE,"E54.bottom"),sQuery(id+"F52.wireOp",EDGE,"E54.top"),sQuery(id+"F52.wireOp",EDGE,"E54.left"),sQuery(id+"F52.wireOp",EDGE,"E54.right")])]}),"instanceName":"1"}),"instanceName":"1"});
            var Q1;
            Q1=makeQuery(id+"F60.opPattern","COPY",VERTEX,{"derivedFrom":makeQuery(id+"F56.opPattern","COPY",VERTEX,{"derivedFrom":makeQuery(id+"F53.opExtrude","CAP_VERTEX",VERTEX,{"disambiguationData":[OSD([sQuery(id+"F52.wireOp",EDGE,"E54.bottom"),sQuery(id+"F52.wireOp",EDGE,"E54.left")])],"isStart":false}),"instanceName":"1"}),"instanceName":"1"});
            transform(context, id + "F61", {"entities" : qUnion([Q0]), "transformType" : TransformType.SCALE_UNIFORMLY, "scale" : .9, "scalePoint" : qUnion([Q1]), "makeCopy" : false});
        }
        {
            var Q0;
            Q0=qCreatedBy(makeId("Top.planeOp"),FACE);
            var sketch = newSketch(context, id + "F62", { "sketchPlane" : qUnion([Q0])});
            skLineSegment(sketch, "E57.bottom", {"start": v(216.38, -3094.6) * mm, "end": v(575.16, -3094.6) * mm});
            skLineSegment(sketch, "E57.top", {"start": v(216.38, -4015.35) * mm, "end": v(575.16, -4015.35) * mm});
            skLineSegment(sketch, "E57.left", {"start": v(216.38, -3094.6) * mm, "end": v(216.38, -4015.35) * mm});
            skLineSegment(sketch, "E57.right", {"start": v(575.16, -3094.6) * mm, "end": v(575.16, -4015.35) * mm});
            skSolve(sketch);
        }
        {
            var Q0;
            Q0 = qSketchRegion(id + "F62", true);
            extrude(context, id + "F63", {"entities" : qUnion([Q0]), "depth" : 1787.52 * mm, "offsetDistance" : 25.4 * mm});
        }
        {
            var Q0;
            Q0=makeQuery(id+"F63.opExtrude","SWEPT_BODY",BODY,{"disambiguationData":[OSD([sQuery(id+"F62.wireOp",EDGE,"E57.bottom"),sQuery(id+"F62.wireOp",EDGE,"E57.top"),sQuery(id+"F62.wireOp",EDGE,"E57.left"),sQuery(id+"F62.wireOp",EDGE,"E57.right")])]});
            transform(context, id + "F64", {"entities" : qUnion([Q0]), "transformType" : TransformType.TRANSLATION_3D, "dx" : -60.96 * mm, "dy" : -71.12 * mm, "dz" : 0 * mm, "makeCopy" : false});
        }
        {
            var Q0;
            Q0=qCreatedBy(makeId("Top.planeOp"),FACE);
            var sketch = newSketch(context, id + "F65", { "sketchPlane" : qUnion([Q0])});
            skLineSegment(sketch, "E58.bottom", {"start": v(2147.1, -2084.28) * mm, "end": v(1588.3, -2084.28) * mm});
            skLineSegment(sketch, "E58.top", {"start": v(2147.1, -2541.48) * mm, "end": v(1588.3, -2541.48) * mm});
            skLineSegment(sketch, "E58.left", {"start": v(2147.1, -2084.28) * mm, "end": v(2147.1, -2541.48) * mm});
            skLineSegment(sketch, "E58.right", {"start": v(1588.3, -2084.28) * mm, "end": v(1588.3, -2541.48) * mm});
            skSolve(sketch);
        }
        {
            var Q0;
            Q0 = qSketchRegion(id + "F65", true);
            extrude(context, id + "F66", {"entities" : qUnion([Q0]), "depth" : 609.6 * mm, "offsetDistance" : 25.4 * mm});
        }
        {
            var Q0;
            Q0=makeQuery(id+"F53.opExtrude","SWEPT_BODY",BODY,{"disambiguationData":[OSD([sQuery(id+"F52.wireOp",EDGE,"E54.bottom"),sQuery(id+"F52.wireOp",EDGE,"E54.top"),sQuery(id+"F52.wireOp",EDGE,"E54.left"),sQuery(id+"F52.wireOp",EDGE,"E54.right")])]});
            var Q1;
            Q1=makeQuery(id+"F53.opExtrude","SWEPT_EDGE",EDGE,{"disambiguationData":[OSD([sQuery(id+"F52.wireOp",EDGE,"E54.top"),sQuery(id+"F52.wireOp",EDGE,"E54.right")])]});
            transform(context, id + "F67", {"entities" : qUnion([Q0]), "transformType" : TransformType.ROTATION, "transformAxis" : qUnion([Q1]), "angle" : 30 * degree, "makeCopy" : false});
        }
        {
            var Q0;
            Q0=makeQuery(id+"F56.opPattern","COPY",BODY,{"derivedFrom":makeQuery(id+"F53.opExtrude","SWEPT_BODY",BODY,{"disambiguationData":[OSD([sQuery(id+"F52.wireOp",EDGE,"E54.bottom"),sQuery(id+"F52.wireOp",EDGE,"E54.top"),sQuery(id+"F52.wireOp",EDGE,"E54.left"),sQuery(id+"F52.wireOp",EDGE,"E54.right")])]}),"instanceName":"1"});
            var Q1;
            Q1=makeQuery(id+"F56.opPattern","COPY",EDGE,{"derivedFrom":makeQuery(id+"F53.opExtrude","SWEPT_EDGE",EDGE,{"disambiguationData":[OSD([sQuery(id+"F52.wireOp",EDGE,"E54.bottom"),sQuery(id+"F52.wireOp",EDGE,"E54.right")])]}),"instanceName":"1"});
            transform(context, id + "F68", {"entities" : qUnion([Q0]), "transformType" : TransformType.ROTATION, "transformAxis" : qUnion([Q1]), "angle" : 330 * degree, "makeCopy" : false});
        }
        {
            var Q0;
            Q0=makeQuery(id+"F56.opPattern","COPY",BODY,{"derivedFrom":makeQuery(id+"F53.opExtrude","SWEPT_BODY",BODY,{"disambiguationData":[OSD([sQuery(id+"F52.wireOp",EDGE,"E54.bottom"),sQuery(id+"F52.wireOp",EDGE,"E54.top"),sQuery(id+"F52.wireOp",EDGE,"E54.left"),sQuery(id+"F52.wireOp",EDGE,"E54.right")])]}),"instanceName":"1"});
            transform(context, id + "F69", {"entities" : qUnion([Q0]), "transformType" : TransformType.TRANSLATION_3D, "dx" : -233.68 * mm, "dy" : -55.88 * mm, "dz" : 0 * mm, "makeCopy" : false});
        }
    });
